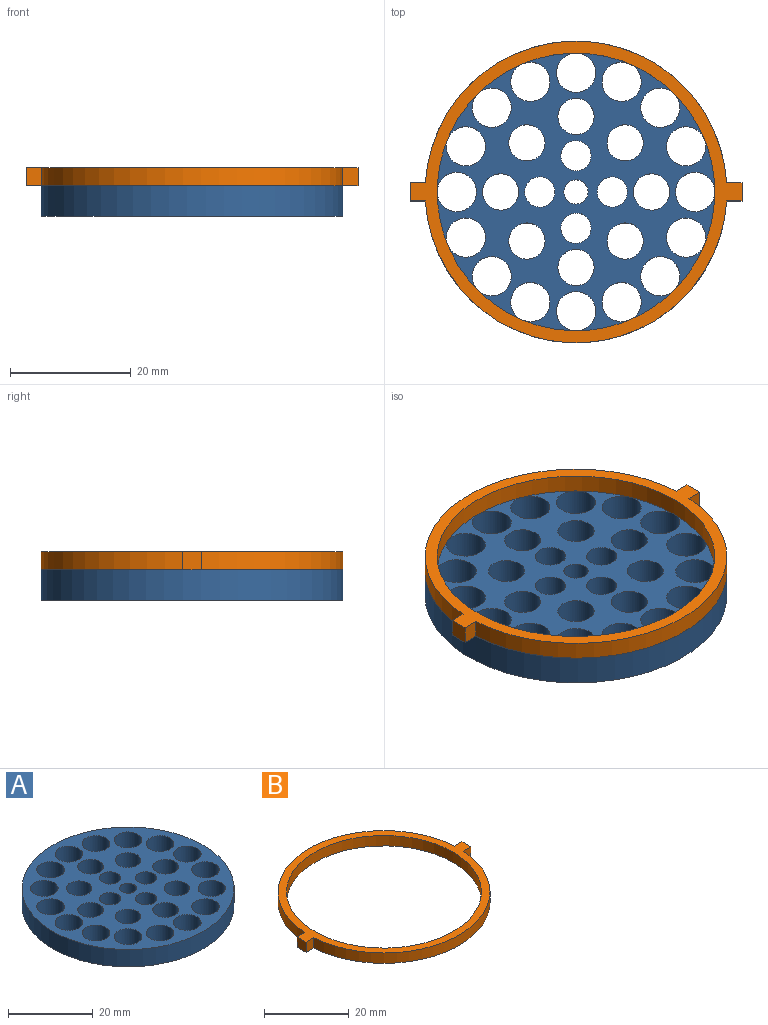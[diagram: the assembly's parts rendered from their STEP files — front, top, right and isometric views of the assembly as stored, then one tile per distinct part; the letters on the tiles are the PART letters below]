
ASSEMBLY  parts=2 mates=1
PART A: 32 faces, bbox 50x50x5 mm
  f0: cylinder r=3.25mm len=6.5mm, axis (0,0,-1), area 102.1mm2, adj f30,f31
  f1: cylinder r=3mm len=6mm, axis (0,0,-1), area 94.2mm2, adj f30,f31
  f2: cylinder r=2.5mm len=5mm, axis (0,0,-1), area 78.5mm2, adj f30,f31
  f3: cylinder r=2mm len=5mm, axis (0,0,-1), area 62.8mm2, adj f30,f31
  f4: cylinder r=2.5mm len=5mm, axis (0,0,-1), area 78.5mm2, adj f30,f31
  f5: cylinder r=3mm len=6mm, axis (0,0,-1), area 94.2mm2, adj f30,f31
  f6: cylinder r=3.25mm len=6.5mm, axis (0,0,-1), area 102.1mm2, adj f30,f31
  f7: cylinder r=2.5mm len=5mm, axis (0,0,-1), area 78.5mm2, adj f30,f31
  f8: cylinder r=3mm len=6mm, axis (0,0,-1), area 94.2mm2, adj f30,f31
  f9: cylinder r=3.25mm len=6.5mm, axis (0,0,-1), area 102.1mm2, adj f30,f31
  f10: cylinder r=2.5mm len=5mm, axis (0,0,-1), area 78.5mm2, adj f30,f31
  f11: cylinder r=3mm len=6mm, axis (0,0,-1), area 94.2mm2, adj f30,f31
  f12: cylinder r=3.25mm len=6.5mm, axis (0,0,-1), area 102.1mm2, adj f30,f31
  f13: cylinder r=3.25mm len=6.5mm, axis (0,0,-1), area 102.1mm2, adj f30,f31
  f14: cylinder r=3.25mm len=6.5mm, axis (0,0,-1), area 102.1mm2, adj f30,f31
  f15: cylinder r=3.25mm len=6.5mm, axis (0,0,-1), area 102.1mm2, adj f30,f31
  f16: cylinder r=3.25mm len=6.5mm, axis (0,0,-1), area 102.1mm2, adj f30,f31
  f17: cylinder r=3mm len=6mm, axis (0,0,-1), area 94.2mm2, adj f30,f31
  f18: cylinder r=3mm len=6mm, axis (0,0,-1), area 94.2mm2, adj f30,f31
  f19: cylinder r=3mm len=6mm, axis (0,0,-1), area 94.2mm2, adj f30,f31
  f20: cylinder r=3mm len=6mm, axis (0,0,-1), area 94.2mm2, adj f30,f31
  f21: cylinder r=3.25mm len=6.5mm, axis (0,0,-1), area 102.1mm2, adj f30,f31
  f22: cylinder r=3.25mm len=6.5mm, axis (0,0,-1), area 102.1mm2, adj f30,f31
  f23: cylinder r=3.25mm len=6.5mm, axis (0,0,-1), area 102.1mm2, adj f30,f31
  f24: cylinder r=3.25mm len=6.5mm, axis (0,0,-1), area 102.1mm2, adj f30,f31
  f25: cylinder r=3.25mm len=6.5mm, axis (0,0,-1), area 102.1mm2, adj f30,f31
  f26: cylinder r=3.25mm len=6.5mm, axis (0,0,-1), area 102.1mm2, adj f30,f31
  f27: cylinder r=3.25mm len=6.5mm, axis (0,0,-1), area 102.1mm2, adj f30,f31
  f28: cylinder r=3.25mm len=6.5mm, axis (0,0,-1), area 102.1mm2, adj f30,f31
  f29: cylinder r=25mm len=50mm, axis (0,0,-1), area 785.4mm2, adj f30,f31
  f30: plane 50x50mm, normal (0,0,1), area 1115.3mm2, adj f0,f1,f2,f3,f4,f5,f6,f7
  f31: plane 50x50mm, normal (0,0,-1), area 1115.3mm2, adj f0,f1,f2,f3,f4,f5,f6,f7
PART B: 11 faces, bbox 55x50x3 mm
  f0: plane 3x2.55mm, normal (0,1,0), area 7.6mm2, adj f1,f7,f9,f10
  f1: cylinder r=25mm len=49.91mm, axis (0,0,-1), area 226.6mm2, adj f0,f2,f9,f10
  f2: plane 3x2.55mm, normal (0,1,0), area 7.6mm2, adj f1,f3,f9,f10
  f3: plane 3x3mm, normal (-1,0,0), area 9mm2, adj f2,f4,f9,f10
  f4: plane 3x2.55mm, normal (0,-1,0), area 7.6mm2, adj f3,f5,f9,f10
  f5: cylinder r=25mm len=49.91mm, axis (0,0,-1), area 226.6mm2, adj f4,f6,f9,f10
  f6: plane 3x2.55mm, normal (0,-1,0), area 7.6mm2, adj f5,f7,f9,f10
  f7: plane 3x3mm, normal (1,0,0), area 9mm2, adj f0,f6,f9,f10
  f8: cylinder r=23mm len=46mm, axis (0,0,-1), area 433.5mm2, adj f9,f10
  f9: plane 55x50mm, normal (0,0,1), area 316.7mm2, adj f0,f1,f2,f3,f4,f5,f6,f7
  f10: plane 55x50mm, normal (0,0,-1), area 316.7mm2, adj f0,f1,f2,f3,f4,f5,f6,f7
PLACE A t=(-34.19,-9.67,38.8)mm
PLACE B t=(-34.19,-9.67,43.8)mm
MATE fastened A.f3 <-> B.f1  axis (0,0,1) through (-34.19,-9.67,43.8)mm
